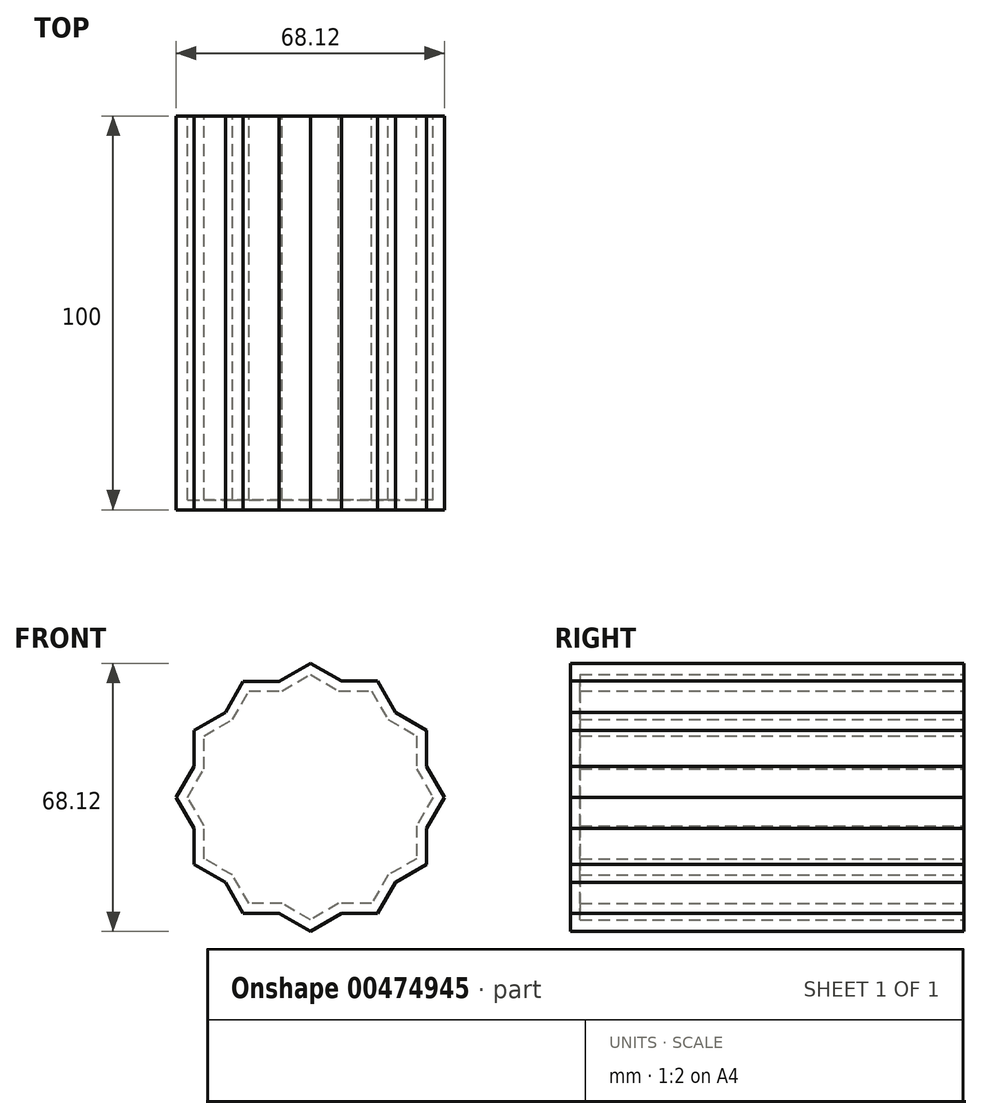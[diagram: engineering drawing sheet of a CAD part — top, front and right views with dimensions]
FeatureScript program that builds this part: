
annotation { "Feature Type Name" : "Feature", "Feature Type Description" : "" }
export const myFeature = defineFeature(function(context is Context, id is Id, definition is map)
    precondition{}
    {
        {
            var Q0;
            Q0=qCreatedBy(makeId("Front.planeOp"),FACE);
            var sketch = newSketch(context, id + "F0", { "sketchPlane" : qUnion([Q0])});
            skCircle(sketch, "E0.cCircle", {"center": v(0, 0) * mm, "radius": 29.5 * mm, "construction": true});
            skLineSegment(sketch, "E0.0", {"start": v(17.03, 29.5) * mm, "end": v(34.06, 0) * mm});
            skLineSegment(sketch, "E0.1", {"start": v(34.06, 0) * mm, "end": v(17.03, -29.5) * mm});
            skLineSegment(sketch, "E0.2", {"start": v(17.03, -29.5) * mm, "end": v(-17.03, -29.5) * mm});
            skLineSegment(sketch, "E0.3", {"start": v(-17.03, -29.5) * mm, "end": v(-34.06, 0) * mm});
            skLineSegment(sketch, "E0.4", {"start": v(-34.06, 0) * mm, "end": v(-17.03, 29.5) * mm});
            skLineSegment(sketch, "E0.5", {"start": v(-17.03, 29.5) * mm, "end": v(17.03, 29.5) * mm});
            skPoint(sketch, "E0.0.midPoint", {"position": v(25.55, 14.75) * mm});
            skLineSegment(sketch, "E1.0", {"start": v(0, -34.06) * mm, "end": v(-29.5, -17.03) * mm});
            skLineSegment(sketch, "E1.1", {"start": v(-29.5, -17.03) * mm, "end": v(-29.5, 17.03) * mm});
            skLineSegment(sketch, "E1.2", {"start": v(-29.5, 17.03) * mm, "end": v(0, 34.06) * mm});
            skLineSegment(sketch, "E1.3", {"start": v(0, 34.06) * mm, "end": v(29.5, 17.03) * mm});
            skLineSegment(sketch, "E1.4", {"start": v(29.5, 17.03) * mm, "end": v(29.5, -17.03) * mm});
            skLineSegment(sketch, "E1.5", {"start": v(29.5, -17.03) * mm, "end": v(0, -34.06) * mm});
            skPoint(sketch, "E1.0.midPoint", {"position": v(-14.75, -25.55) * mm});
            skSolve(sketch);
        }
        {
            var Q0;
            Q0 = qSketchRegion(id + "F0", true);
            extrude(context, id + "F1", {"entities" : qUnion([Q0]), "depth" : 100 * mm});
        }
        {
            var Q0;
            Q0=makeQuery(id+"F1.opExtrude","CAP_FACE",FACE,{"disambiguationData":[OSD([sQuery(id+"F0.wireOp",EDGE,"E0.0"),sQuery(id+"F0.wireOp",EDGE,"E0.1"),sQuery(id+"F0.wireOp",EDGE,"E0.2"),sQuery(id+"F0.wireOp",EDGE,"E0.3"),sQuery(id+"F0.wireOp",EDGE,"E0.4"),sQuery(id+"F0.wireOp",EDGE,"E0.5"),sQuery(id+"F0.wireOp",EDGE,"E1.0"),sQuery(id+"F0.wireOp",EDGE,"E1.1"),sQuery(id+"F0.wireOp",EDGE,"E1.2"),sQuery(id+"F0.wireOp",EDGE,"E1.3"),sQuery(id+"F0.wireOp",EDGE,"E1.4"),sQuery(id+"F0.wireOp",EDGE,"E1.5")])],"isStart":true});
            shell(context, id + "F2", {"entities" : qUnion([Q0]), "thickness" : 2.5 * mm});
        }
    });
